# Revit family: Shower-Shower_Trim-STERLING-Medley-TS27372
name_source: partatom
category: Plumbing Fixtures
units: mm (PartAtom-declared; Revit-internal decimal feet)

## family parameters
Cut with Voids When Loaded = No
Host = Face
Maintain Annotation Orientation = No
OmniClass Number = 23.31.17.00
Part Type = Normal
Room Calculation Point = No
Round Connector Dimension = Use Diameter
Shared = No

## types (3) — shared parameters
ADA Compliant = No
Assembly Code = D2010700
CW Connection = No
Cold Water Inlet = Cold Water Inlet
Date Modified = 04/21/2025
Default Elevation = 42"
Description = Rite Temp Shower Trim
Drain Included = No
Flow Rate = 2 GPM
HW Connection = Yes
Handle Clearance = 2 15/16"
Height = 6"
Hot Water Inlet = Hot Water Inlet
Length = 7 5/16"
Manufacturer = Sterling Co.
Master Format 2014 = 22 42 23
Master Format 2014 Name = Residential Showers
Material = Premium Metal Construction
Pressure = 45.00 psi
Product Documentation Link = https://resources.kohler.com
Product Name = Medley
Product Page URL = http://www.sterlingplumbing.com
Tempered Water Inlet = Tempered Water Inlet
URL = https://www.sterlingplumbing.com
Vent Connection = No
Waste Connection = No
Waste Water Outlet = Waste Water Outlet
WaterSense Certified = No
Width = 6"

## per-type parameters (varying)
| type | Finish | Model | Type |
| CP-Polished Chrome | Sterling-Metal-CP-Polished_Chrome | TS27372-4G-CP | 1 |
| BL-Matte Black | Sterling-Metal-BL-Matte_Black | TS27372-4G-BL | 2 |
| BN-Vibrant Brushed Nickel | Sterling-Metal-BN-Vibrant_Brushed_Nickel | TS27372-4G-BN | 3 |

## geometry (parser evidence)
native form markers: Sweep x11
no freeform markers — native parametric forms only
